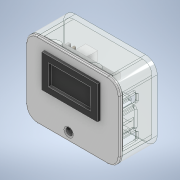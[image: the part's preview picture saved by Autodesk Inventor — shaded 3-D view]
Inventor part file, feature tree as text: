
AUTODESK INVENTOR PART (.ipt)
format: ipt  version: 2022 (Build 260153000, 153)  size: 791,552 bytes
history: native  units: in
note: dims shown in document units (in); Inventor stores cm internally (conversion verified against a paired STEP export)
features: extrude x18, sketch x18, fillet x6, other x4, plane x1
ambient origin geometry x8: Origin, YZ Plane, XZ Plane, XY Plane, X Axis, Y Axis, Z Axis, Center Point
bodies: Body1 (feature_tree), Body2 (feature_tree), Body3 (feature_tree), Body4 (feature_tree)
feature tree (47):
  other  "Faceplate"
  extrude  "Front Panel Blank"  Depth=2.5591in
  extrude  "Voltmeter Screen"  Depth=1.5748in
  extrude  "Extrusion45"  Depth=0.3937in TaperAngle=0.0deg
  extrude  "Extrusion46"  Depth=0.5906in
  extrude  "Extrusion47"  Depth=0.0197in
  extrude  "Extrusion48"  Depth=0.0197in
  extrude  "Extrusion49"  Depth=1.0236in
  extrude  "Extrusion50"  Depth=0.3937in
  fillet  "Fillet36"  Radius=0.1969in
  fillet  "Fillet37"  Radius=0.3937in
  extrude  "Extrusion51"  Depth=0.0906in
  extrude  "Extrusion52"  Depth=0.0787in
  extrude  "Extrusion53"  Depth=0.0295in
  plane  "Work Plane2"
  extrude  "PSU PCB"  Depth=0.0551in
  extrude  "Extrusion55"  Depth=0.2323in
  extrude  "Extrusion56"  Depth=0.2087in
  extrude  "Extrusion57"  Depth=0.0984in TaperAngle=0.0deg
  extrude  "Extrusion58"  Depth=0.3937in
  extrude  "Extrusion59"  Depth=0.3937in
  fillet  "Fillet38"  Radius=0.0079in
  fillet  "Fillet39"  Radius=0.5748in
  fillet  "Fillet40"  Radius=0.0591in
  fillet  "Fillet41"  Radius=0.0591in
  extrude  "Extrusion60"  Depth=0.3937in
  sketch  "Sketch1"  dims[d0=3.1496in d1=2.5591in]
  sketch  "Sketch3"  dims[d2=1.2795in d4=1.5748in]
  sketch  "Sketch59"  dims[d5=0.3937in d6=0.0984in d7=0.0in]
  other  "Screen"
  sketch  "Sketch60"  dims[d30=1.7717in d31=0.5906in d32=1.0236in d33=0.8858in]
  sketch  "Sketch61"  dims[d34=0.9449in d35=0.4724in d36=0.0197in d37=0.0197in]
  sketch  "Sketch64"  dims[d38=0.0197in d39=0.0197in]
  sketch  "Sketch65"  dims[d40=0.9449in d43=1.0236in]
  sketch  "Sketch66"  dims[d44=0.4724in d45=1.063in d46=0.1969in d47=0.0in d85=0.3937in]
  sketch  "Sketch67"  dims[d161=0.315in d270=0.0906in]
  sketch  "Sketch68"  dims[d377=1.1024in d380=0.7283in d381=0.0787in d386=0.0394in]
  sketch  "Sketch70"  dims[d481=0.0in d488=0.0in d489=0.0in d491=0.1772in d492=0.1772in]
  other  "Box"
  sketch  "Sketch71"  dims[d688=0.0394in d689=0.2953in d690=0.0394in d691=0.1181in d701=0.1732in d702=0.1772in d704=0.0787in d705=0.0787in d811=1.8819in]
  other  "PSU"
  sketch  "Sketch72"  dims[d812=1.122in d814=0.0295in]
  sketch  "Sketch73"  dims[d815=0.0295in d816=0.0551in]
  sketch  "Sketch74"  dims[d817=0.0551in d819=0.2323in]
  sketch  "Sketch75"  dims[d820=0.2323in d821=0.2087in]
  sketch  "Sketch76"  dims[d822=0.2087in d823=0.0984in d824=0.0in]
  sketch  "Sketch77"  dims[d825=0.0079in d826=0.0079in d827=0.0079in d828=0.0079in d829=0.5748in d830=0.0in d831=0.0591in d832=0.0591in d833=0.25in d834=0.25in d835=0.0831in d836=0.0831in d837=0.1669in d838=0.0in d839=0.4024in d840=0.3165in d841=0.2756in d842=0.1181in d843=0.4724in d844=0.0in d845=0.3937in d846=0.2205in d847=0.4921in d848=0.3386in d849=0.2008in d850=0.0in d851=0.4764in d852=0.0846in d853=0.1969in d854=0.5906in d855=0.248in d856=0.0in d857=0.0413in d858=0.0394in d859=0.4331in d860=0.4331in d862=0.4331in d863=0.4331in d864=0.1575in d865=0.1575in d866=0.1575in d867=0.1575in d868=0.0984in d869=0.0984in d870=0.0984in d871=0.0984in d872=0.1181in d873=0.0in d874=0.3937in d875=0.315in d876=1.1024in d877=0.0in d881=0.3937in d882=0.0787in d883=0.0in d884=0.8386in d885=1.7126in d886=0.6201in d887=0.6201in d888=0.1181in d889=0.3508in d890=0.0in d891=0.089in d892=0.0638in d893=0.726in d894=0.1614in d895=0.0in d896=0.1181in d897=0.1181in d898=0.1181in d899=0.1181in d900=0.1181in d901=0.0787in d902=0.0787in d903=0.0787in d904=0.7874in d905=0.0in d906=0.2362in d907=0.2362in d908=0.0in d910=0.315in d911=0.0in d912=0.0in d913=0.0in d914=0.1969in d915=0.1181in d916=0.1181in d917=0.1181in d918=0.1181in d919=0.1969in d920=0.5906in d921=0.0in d922=0.6201in d923=0.6201in d924=0.1181in d925=0.8386in d926=0.5906in d927=0.0394in d928=0.0394in d929=0.5906in d930=0.2756in d931=0.5906in d932=0.2756in d933=0.0394in d934=0.0394in d935=0.5118in d936=0.0in d937=0.0394in d938=0.0394in d939=0.0394in d940=0.0394in d941=0.9055in d942=0.9055in d943=0.9055in d944=0.9055in d945=0.3937in d951=0.9055in d952=0.9055in d953=0.3937in d954=0.5118in d955=-0.0687in]
